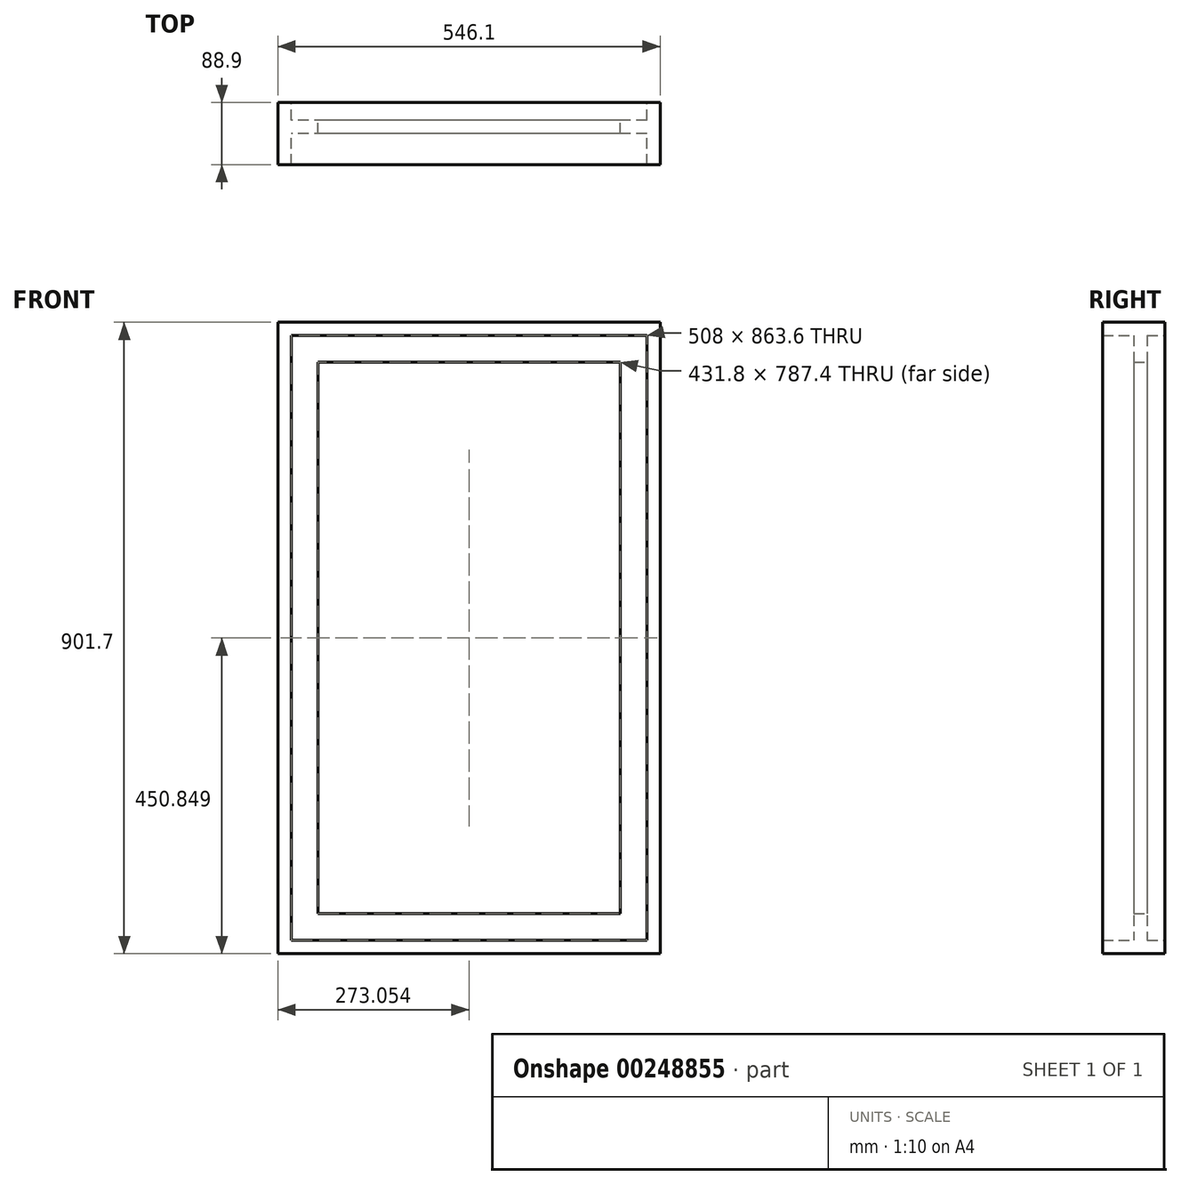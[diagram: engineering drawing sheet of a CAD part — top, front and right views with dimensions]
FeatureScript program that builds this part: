
annotation { "Feature Type Name" : "Feature", "Feature Type Description" : "" }
export const myFeature = defineFeature(function(context is Context, id is Id, definition is map)
    precondition{}
    {
        {
            var Q0;
            Q0=qCreatedBy(makeId("Front.planeOp"),FACE);
            var sketch = newSketch(context, id + "F0", { "sketchPlane" : qUnion([Q0])});
            skLineSegment(sketch, "E0", {"start": v(-303.09, 588.55) * mm, "end": v(-303.09, -313.15) * mm});
            skLineSegment(sketch, "E1", {"start": v(-303.09, -313.15) * mm, "end": v(243.01, -313.15) * mm});
            skLineSegment(sketch, "E2", {"start": v(243.01, -313.15) * mm, "end": v(243.01, 588.55) * mm});
            skLineSegment(sketch, "E3", {"start": v(243.01, 588.55) * mm, "end": v(-303.09, 588.55) * mm});
            skLineSegment(sketch, "E4", {"start": v(-284.04, 569.5) * mm, "end": v(-284.04, -294.1) * mm});
            skLineSegment(sketch, "E5", {"start": v(-284.04, -294.1) * mm, "end": v(223.96, -294.1) * mm});
            skLineSegment(sketch, "E6", {"start": v(223.96, -294.1) * mm, "end": v(223.96, 569.5) * mm});
            skLineSegment(sketch, "E7", {"start": v(223.96, 569.5) * mm, "end": v(-284.04, 569.5) * mm});
            skLineSegment(sketch, "E8", {"start": v(-284.04, -294.1) * mm, "end": v(-303.09, -313.15) * mm});
            skLineSegment(sketch, "E9", {"start": v(223.96, -294.1) * mm, "end": v(243.01, -313.15) * mm});
            skLineSegment(sketch, "E10", {"start": v(223.96, 569.5) * mm, "end": v(243.01, 588.55) * mm});
            skLineSegment(sketch, "E11", {"start": v(-284.04, 569.5) * mm, "end": v(-303.09, 588.55) * mm});
            skLineSegment(sketch, "E12", {"start": v(-245.94, 531.4) * mm, "end": v(-245.94, -256) * mm});
            skLineSegment(sketch, "E13", {"start": v(-245.94, -256) * mm, "end": v(185.86, -256) * mm});
            skLineSegment(sketch, "E14", {"start": v(185.86, -256) * mm, "end": v(185.86, 531.4) * mm});
            skLineSegment(sketch, "E15", {"start": v(185.86, 531.4) * mm, "end": v(-245.94, 531.4) * mm});
            skLineSegment(sketch, "E16", {"start": v(-284.04, 569.5) * mm, "end": v(-245.94, 531.4) * mm});
            skLineSegment(sketch, "E17", {"start": v(185.86, 531.4) * mm, "end": v(223.96, 569.5) * mm});
            skLineSegment(sketch, "E18", {"start": v(185.86, -256) * mm, "end": v(223.96, -294.1) * mm});
            skLineSegment(sketch, "E19", {"start": v(-245.94, -256) * mm, "end": v(-284.04, -294.1) * mm});
            skSolve(sketch);
        }
        {
            var Q0;
            Q0 = qSketchRegion(id + "F0", true);
            extrude(context, id + "F1", {"entities" : qUnion([Q0]), "depth" : 88.9 * mm});
        }
        {
            var Q0;
            Q0=makeQuery(id+"F0.imprint","IMPRINT",FACE,{"disambiguationData":[TD([[makeQuery(id+"F0.imprint","IMPRINT",EDGE,{"derivedFrom":sQuery(id+"F0.wireOp",EDGE,"E7")}),1.0]])]});
            var Q1;
            Q1=makeQuery(id+"F0.imprint","IMPRINT",FACE,{"disambiguationData":[TD([[makeQuery(id+"F0.imprint","IMPRINT",EDGE,{"derivedFrom":sQuery(id+"F0.wireOp",EDGE,"E4")}),1.0]])]});
            var Q2;
            Q2=makeQuery(id+"F0.imprint","IMPRINT",FACE,{"disambiguationData":[TD([[makeQuery(id+"F0.imprint","IMPRINT",EDGE,{"derivedFrom":sQuery(id+"F0.wireOp",EDGE,"E6")}),1.0]])]});
            var Q3;
            Q3=makeQuery(id+"F0.imprint","IMPRINT",FACE,{"disambiguationData":[TD([[makeQuery(id+"F0.imprint","IMPRINT",EDGE,{"derivedFrom":sQuery(id+"F0.wireOp",EDGE,"E5")}),1.0]])]});
            extrude(context, id + "F2", {"entities" : qUnion([Q0, Q1, Q2, Q3]), "operationType" : NewBodyOperationType.ADD, "depth" : 44.45 * mm, "hasSecondDirection" : true, "secondDirectionOppositeDirection" : false, "secondDirectionDepth" : 25.4 * mm});
        }
    });
